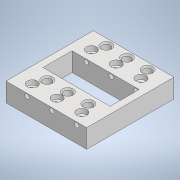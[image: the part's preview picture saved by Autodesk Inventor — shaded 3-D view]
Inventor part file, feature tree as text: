
AUTODESK INVENTOR PART (.ipt)
format: ipt  version: 2022 (Build 260153000, 153)  size: 672,256 bytes
history: native  units: mm
features: sketch x7, other x5, plane x3, pattern_linear x3, extrude x3, projected_geometry x3, loft x2, direct_edit x2, move_body x2, mirror x1, chamfer x1, sweep x1
ambient origin geometry x8: Origin, YZ Plane, XZ Plane, XY Plane, X Axis, Y Axis, Z Axis, Center Point
bodies: Solid1 (feature_tree)
feature tree (33):
  loft  "Loft1"
  plane  "Work Plane1"
  mirror  "Mirror1"
  loft  "Loft2"
  pattern_linear  "Rectangular Pattern1"  Count1=2 Spacing1=88.0mm
  chamfer  "Chamfer1"  Distance=2.0mm Angle=45.0deg
  sketch  "Sketch3"  dims[d8=0.0mm d9=90.0deg d10=20.0mm d12=88.0mm d13=2.0mm d14=2.0mm d15=45.0deg]
  extrude  "Extrusion1"  Depth=8.0mm
  other  "Work Point1"
  other  "Work Point2"
  plane  "Work Plane2"
  sweep  "Sweep1"
  pattern_linear  "Rectangular Pattern3"  Spacing1=0.0mm  [1 undecoded]
  direct_edit  "Direct Edit1"
  direct_edit  "Direct Edit2"
  plane  "Work Plane3"
  extrude  "Extrusion2"  Depth=10.0mm
  pattern_linear  "Rectangular Pattern4"  Spacing1=2.0mm  [1 undecoded]
  extrude  "Extrusion3"  TaperAngle=0.0deg  [1 undecoded]
  sketch  "Sketch1"  dims[d0=7.0mm d1=0.0mm d2=90.0deg d3=0.0mm d4=90.0deg]
  other  "Edges1"
  sketch  "Sketch2"  dims[d5=7.0mm d6=0.0mm d7=90.0deg]
  other  "Edges2"
  sketch  "Sketch5"  dims[d16=6.5mm d17=8.0mm]
  projected_geometry  "Projected Loop1"
  projected_geometry  "Projected Loop2"
  sketch  "Sketch6"  dims[d30=5.0mm d31=5.0mm]
  sketch  "Sketch7"  dims[d32=10.0mm]
  sketch  "Sketch8"  dims[d33=10.0mm d34=0.0mm d35=0.0mm d37=2.0mm d38=2.0mm d39=0.0mm d40=0.0mm d41=30.0mm d43=37.0mm d44=20.0mm d46=88.0mm d47=0.0mm d48=0.0mm d49=-2.0mm d50=0.0mm d51=0.0mm d52=3.0mm d53=29.0mm d54=12.0mm d55=0.0mm d56=20.0mm d58=88.0mm d59=30.0mm d61=37.0mm d62=2.0mm d63=0.0mm]
  projected_geometry  "Projected Loop3"
  other  "Cut-Extrude8"
  move_body  "Move1"
  move_body  "Move2"
note: 3 required parameter values undecoded (feature->parameter linkage not recoverable at this tier; creation-order binding heuristic only, values carry confidence <= 0.55)
